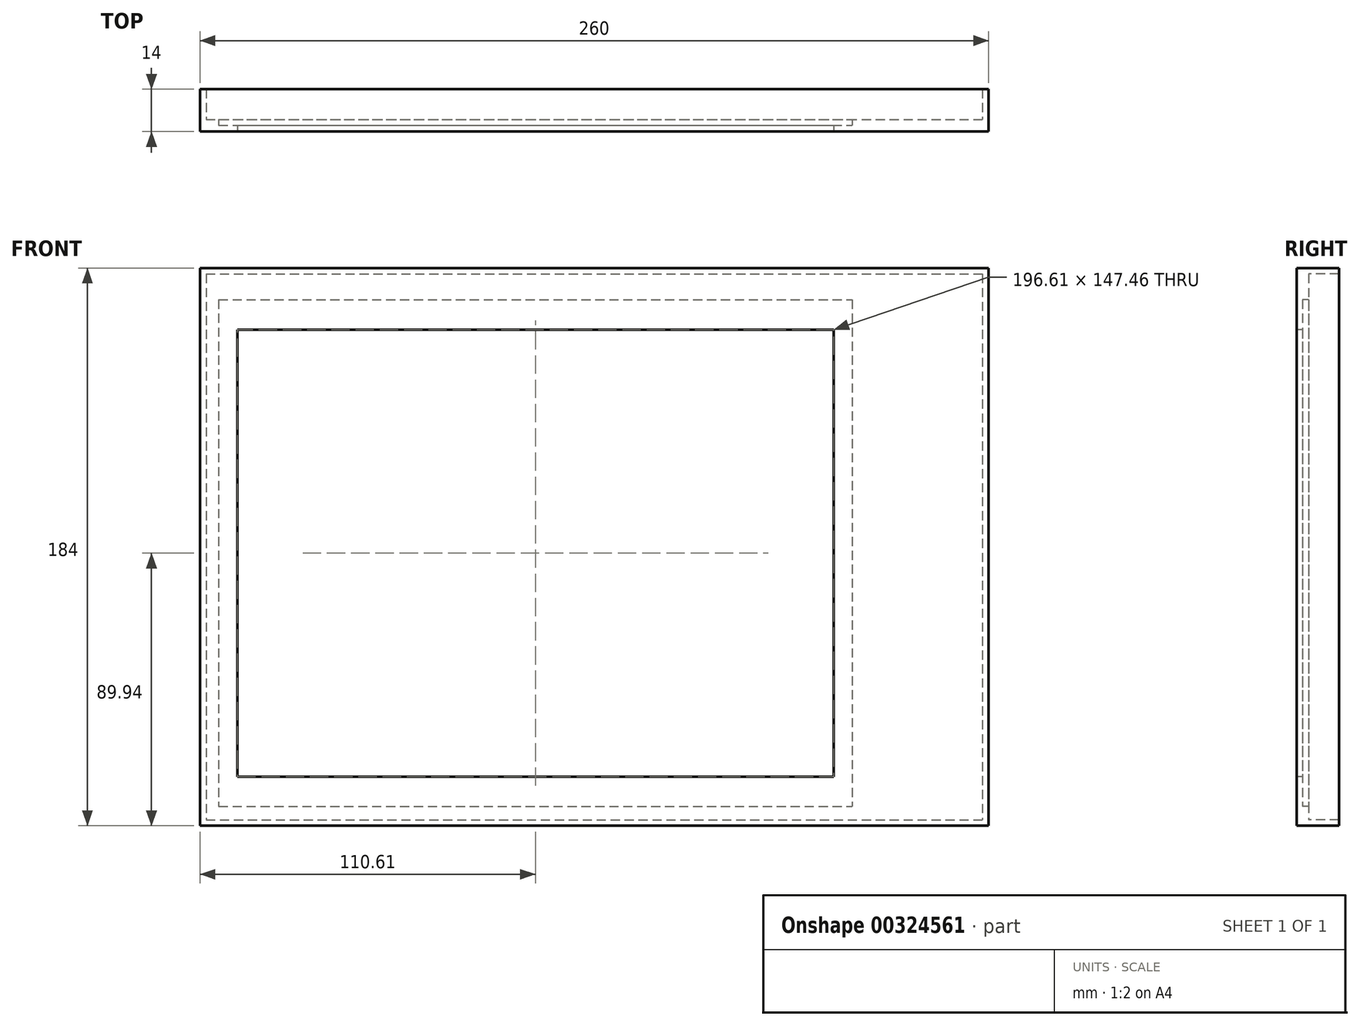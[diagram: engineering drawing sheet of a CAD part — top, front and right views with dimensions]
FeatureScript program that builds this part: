
annotation { "Feature Type Name" : "Feature", "Feature Type Description" : "" }
export const myFeature = defineFeature(function(context is Context, id is Id, definition is map)
    precondition{}
    {
        {
            var Q0;
            Q0=qCreatedBy(makeId("Front.planeOp"),FACE);
            var sketch = newSketch(context, id + "F0", { "sketchPlane" : qUnion([Q0])});
            skLineSegment(sketch, "E0.bottom", {"start": v(-98.3, 73.73) * mm, "end": v(98.3, 73.73) * mm});
            skLineSegment(sketch, "E0.top", {"start": v(-98.3, -73.73) * mm, "end": v(98.3, -73.73) * mm});
            skLineSegment(sketch, "E0.left", {"start": v(-98.3, 73.73) * mm, "end": v(-98.3, -73.73) * mm});
            skLineSegment(sketch, "E0.right", {"start": v(98.3, 73.73) * mm, "end": v(98.3, -73.73) * mm});
            skPoint(sketch, "E0.middle", {"position": v(0, 0) * mm});
            skLineSegment(sketch, "E1.bottom", {"start": v(-108.6, 92.06) * mm, "end": v(147.4, 92.06) * mm});
            skLineSegment(sketch, "E1.top", {"start": v(-108.6, -87.94) * mm, "end": v(147.4, -87.94) * mm});
            skLineSegment(sketch, "E1.left", {"start": v(-108.6, 92.06) * mm, "end": v(-108.6, -87.94) * mm});
            skLineSegment(sketch, "E1.right", {"start": v(147.4, 92.06) * mm, "end": v(147.4, -87.94) * mm});
            skLineSegment(sketch, "E2.bottom", {"start": v(-104.44, 83.56) * mm, "end": v(104.44, 83.56) * mm});
            skLineSegment(sketch, "E2.top", {"start": v(-104.44, -83.56) * mm, "end": v(104.44, -83.56) * mm});
            skLineSegment(sketch, "E2.left", {"start": v(-104.44, 83.56) * mm, "end": v(-104.44, -83.56) * mm});
            skLineSegment(sketch, "E2.right", {"start": v(104.44, 83.56) * mm, "end": v(104.44, -83.56) * mm});
            skLineSegment(sketch, "E3.bottom", {"start": v(-110.6, 94.06) * mm, "end": v(149.4, 94.06) * mm});
            skLineSegment(sketch, "E3.top", {"start": v(-110.6, -89.94) * mm, "end": v(149.4, -89.94) * mm});
            skLineSegment(sketch, "E3.left", {"start": v(-110.6, 94.06) * mm, "end": v(-110.6, -89.94) * mm});
            skLineSegment(sketch, "E3.right", {"start": v(149.4, 94.06) * mm, "end": v(149.4, -89.94) * mm});
            skSolve(sketch);
        }
        {
            var Q0;
            Q0 = qSketchRegion(id + "F0", true);
            extrude(context, id + "F1", {"entities" : qUnion([Q0]), "depth" : -14 * mm});
        }
        {
            var Q0;
            Q0=makeQuery(id+"F0.imprint","IMPRINT",FACE,{"disambiguationData":[TD([[makeQuery(id+"F0.imprint","IMPRINT",EDGE,{"derivedFrom":sQuery(id+"F0.wireOp",EDGE,"E1.bottom")}),-1.0]])]});
            extrude(context, id + "F2", {"entities" : qUnion([Q0]), "operationType" : NewBodyOperationType.ADD, "depth" : -4 * mm});
        }
        {
            var Q0;
            Q0=makeQuery(id+"F0.imprint","IMPRINT",FACE,{"disambiguationData":[TD([[makeQuery(id+"F0.imprint","IMPRINT",EDGE,{"derivedFrom":sQuery(id+"F0.wireOp",EDGE,"E0.bottom")}),1.0]])]});
            extrude(context, id + "F3", {"entities" : qUnion([Q0]), "operationType" : NewBodyOperationType.ADD, "depth" : -2 * mm});
        }
    });
